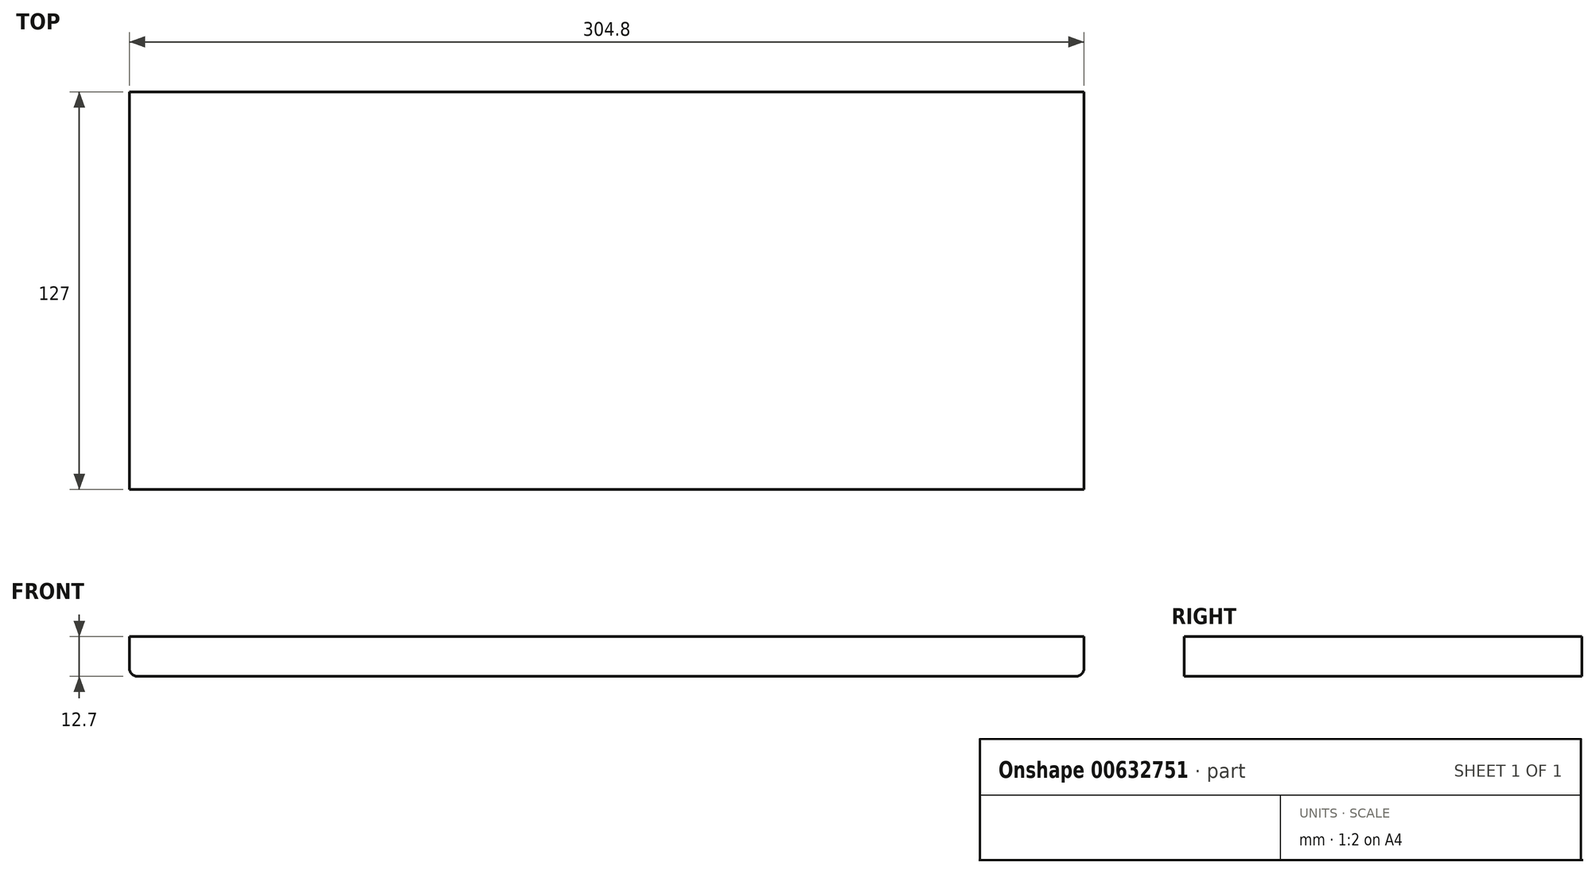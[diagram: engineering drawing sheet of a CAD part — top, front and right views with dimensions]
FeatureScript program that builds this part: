
annotation { "Feature Type Name" : "Feature", "Feature Type Description" : "" }
export const myFeature = defineFeature(function(context is Context, id is Id, definition is map)
    precondition{}
    {
        {
            var Q0;
            Q0=qCreatedBy(makeId("Front.planeOp"),FACE);
            var sketch = newSketch(context, id + "F0", { "sketchPlane" : qUnion([Q0])});
            skLineSegment(sketch, "E0.bottom", {"start": v(-152.4, 6.35) * mm, "end": v(152.4, 6.35) * mm});
            skLineSegment(sketch, "E0.top", {"start": v(-152.4, -6.35) * mm, "end": v(152.4, -6.35) * mm});
            skLineSegment(sketch, "E0.left", {"start": v(-152.4, 6.35) * mm, "end": v(-152.4, -6.35) * mm});
            skLineSegment(sketch, "E0.right", {"start": v(152.4, 6.35) * mm, "end": v(152.4, -6.35) * mm});
            skPoint(sketch, "E0.middle", {"position": v(0, 0) * mm});
            skSolve(sketch);
        }
        {
            var Q0;
            Q0=makeQuery(id+"F0.imprint","IMPRINT",FACE,{"disambiguationData":[TD([[makeQuery(id+"F0.imprint","IMPRINT",EDGE,{"derivedFrom":sQuery(id+"F0.wireOp",EDGE,"E0.bottom")}),-1.0]])]});
            extrude(context, id + "F1", {"entities" : qUnion([Q0]), "endBound" : BoundingType.SYMMETRIC, "depth" : 127 * mm, "offsetDistance" : 25.4 * mm});
        }
        {
            var Q0;
            Q0=makeQuery(id+"F1.opExtrude","SWEPT_EDGE",EDGE,{"disambiguationData":[OSD([sQuery(id+"F0.wireOp",EDGE,"E0.top"),sQuery(id+"F0.wireOp",EDGE,"E0.left")])]});
            var Q1;
            Q1=makeQuery(id+"F1.opExtrude","SWEPT_EDGE",EDGE,{"disambiguationData":[OSD([sQuery(id+"F0.wireOp",EDGE,"E0.top"),sQuery(id+"F0.wireOp",EDGE,"E0.right")])]});
            fillet(context, id + "F2", {"entities" : qUnion([Q0, Q1]), "radius" : 2.54 * mm, "tangentPropagation" : true, "allowEdgeOverflow" : false});
        }
    });
